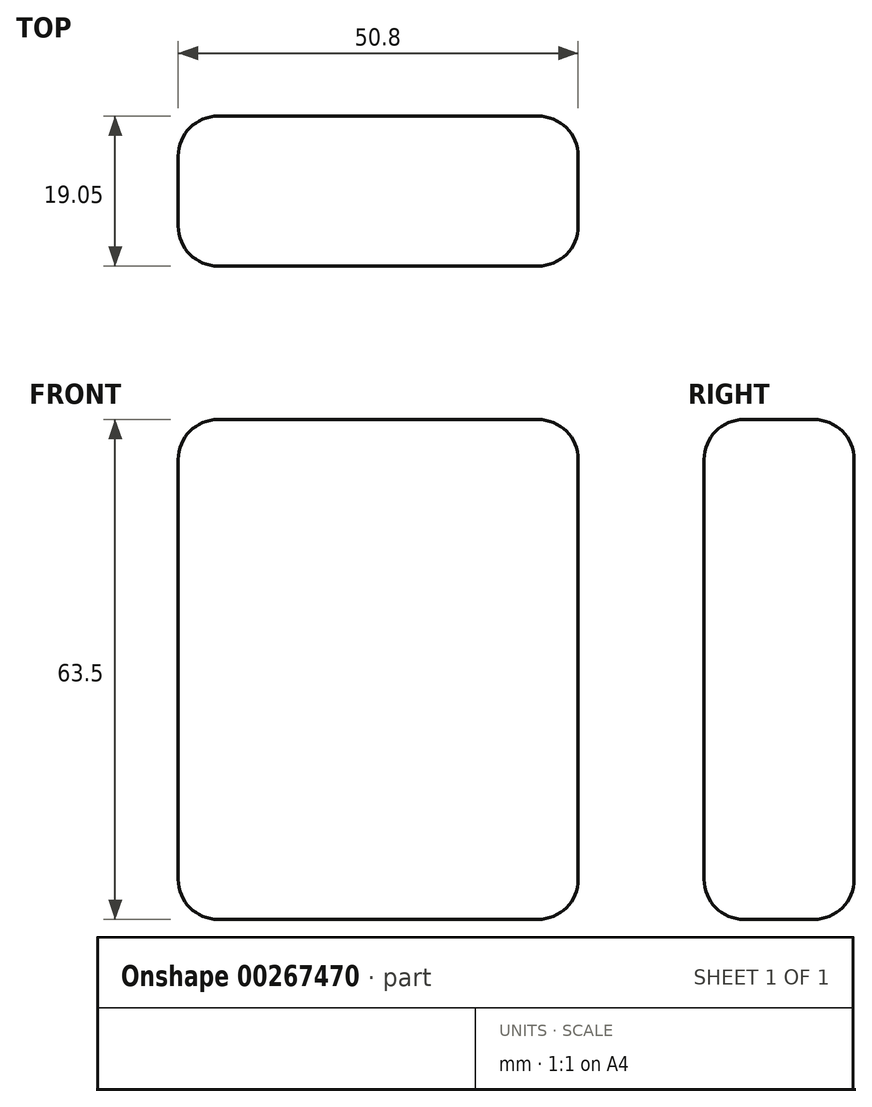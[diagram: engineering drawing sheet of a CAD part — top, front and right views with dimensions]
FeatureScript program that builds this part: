
annotation { "Feature Type Name" : "Feature", "Feature Type Description" : "" }
export const myFeature = defineFeature(function(context is Context, id is Id, definition is map)
    precondition{}
    {
        {
            var Q0;
            Q0=qCreatedBy(makeId("Front.planeOp"),FACE);
            var sketch = newSketch(context, id + "F0", { "sketchPlane" : qUnion([Q0])});
            skLineSegment(sketch, "E0.bottom", {"start": v(-25.4, 31.75) * mm, "end": v(25.4, 31.75) * mm});
            skLineSegment(sketch, "E0.top", {"start": v(-25.4, -31.75) * mm, "end": v(25.4, -31.75) * mm});
            skLineSegment(sketch, "E0.left", {"start": v(-25.4, 31.75) * mm, "end": v(-25.4, -31.75) * mm});
            skLineSegment(sketch, "E0.right", {"start": v(25.4, 31.75) * mm, "end": v(25.4, -31.75) * mm});
            skPoint(sketch, "E0.middle", {"position": v(0, 0) * mm});
            skSolve(sketch);
        }
        {
            var Q0;
            Q0 = qSketchRegion(id + "F0", true);
            extrude(context, id + "F1", {"entities" : qUnion([Q0]), "depth" : 19.05 * mm});
        }
        {
            var Q0;
            Q0=makeQuery(id+"F1.opExtrude","CAP_EDGE",EDGE,{"disambiguationData":[OSD([sQuery(id+"F0.wireOp",EDGE,"E0.left")])],"isStart":false});
            var Q1;
            Q1=makeQuery(id+"F1.opExtrude","CAP_EDGE",EDGE,{"disambiguationData":[OSD([sQuery(id+"F0.wireOp",EDGE,"E0.bottom")])],"isStart":false});
            var Q2;
            Q2=makeQuery(id+"F1.opExtrude","CAP_EDGE",EDGE,{"disambiguationData":[OSD([sQuery(id+"F0.wireOp",EDGE,"E0.right")])],"isStart":false});
            var Q3;
            Q3=makeQuery(id+"F1.opExtrude","CAP_FACE",FACE,{"disambiguationData":[OSD([sQuery(id+"F0.wireOp",EDGE,"E0.bottom"),sQuery(id+"F0.wireOp",EDGE,"E0.top"),sQuery(id+"F0.wireOp",EDGE,"E0.left"),sQuery(id+"F0.wireOp",EDGE,"E0.right")])],"isStart":false});
            var Q4;
            Q4=makeQuery(id+"F1.opExtrude","SWEPT_EDGE",EDGE,{"disambiguationData":[OSD([sQuery(id+"F0.wireOp",EDGE,"E0.top"),sQuery(id+"F0.wireOp",EDGE,"E0.right")])]});
            var Q5;
            Q5=makeQuery(id+"F1.opExtrude","SWEPT_EDGE",EDGE,{"disambiguationData":[OSD([sQuery(id+"F0.wireOp",EDGE,"E0.top"),sQuery(id+"F0.wireOp",EDGE,"E0.left")])]});
            var Q6;
            Q6=makeQuery(id+"F1.opExtrude","SWEPT_EDGE",EDGE,{"disambiguationData":[OSD([sQuery(id+"F0.wireOp",EDGE,"E0.bottom"),sQuery(id+"F0.wireOp",EDGE,"E0.right")])]});
            var Q7;
            Q7=makeQuery(id+"F1.opExtrude","SWEPT_EDGE",EDGE,{"disambiguationData":[OSD([sQuery(id+"F0.wireOp",EDGE,"E0.bottom"),sQuery(id+"F0.wireOp",EDGE,"E0.left")])]});
            fillet(context, id + "F2", {"entities" : qUnion([Q0, Q1, Q2, Q3, Q4, Q5, Q6, Q7]), "radius" : 5.08 * mm, "tangentPropagation" : true, "allowEdgeOverflow" : false});
        }
        {
            var Q0;
            Q0=makeQuery(id+"F1.opExtrude","CAP_EDGE",EDGE,{"disambiguationData":[OSD([sQuery(id+"F0.wireOp",EDGE,"E0.left")])],"isStart":true});
            fillet(context, id + "F3", {"entities" : qUnion([Q0]), "radius" : 5.08 * mm, "tangentPropagation" : true, "allowEdgeOverflow" : false});
        }
    });
